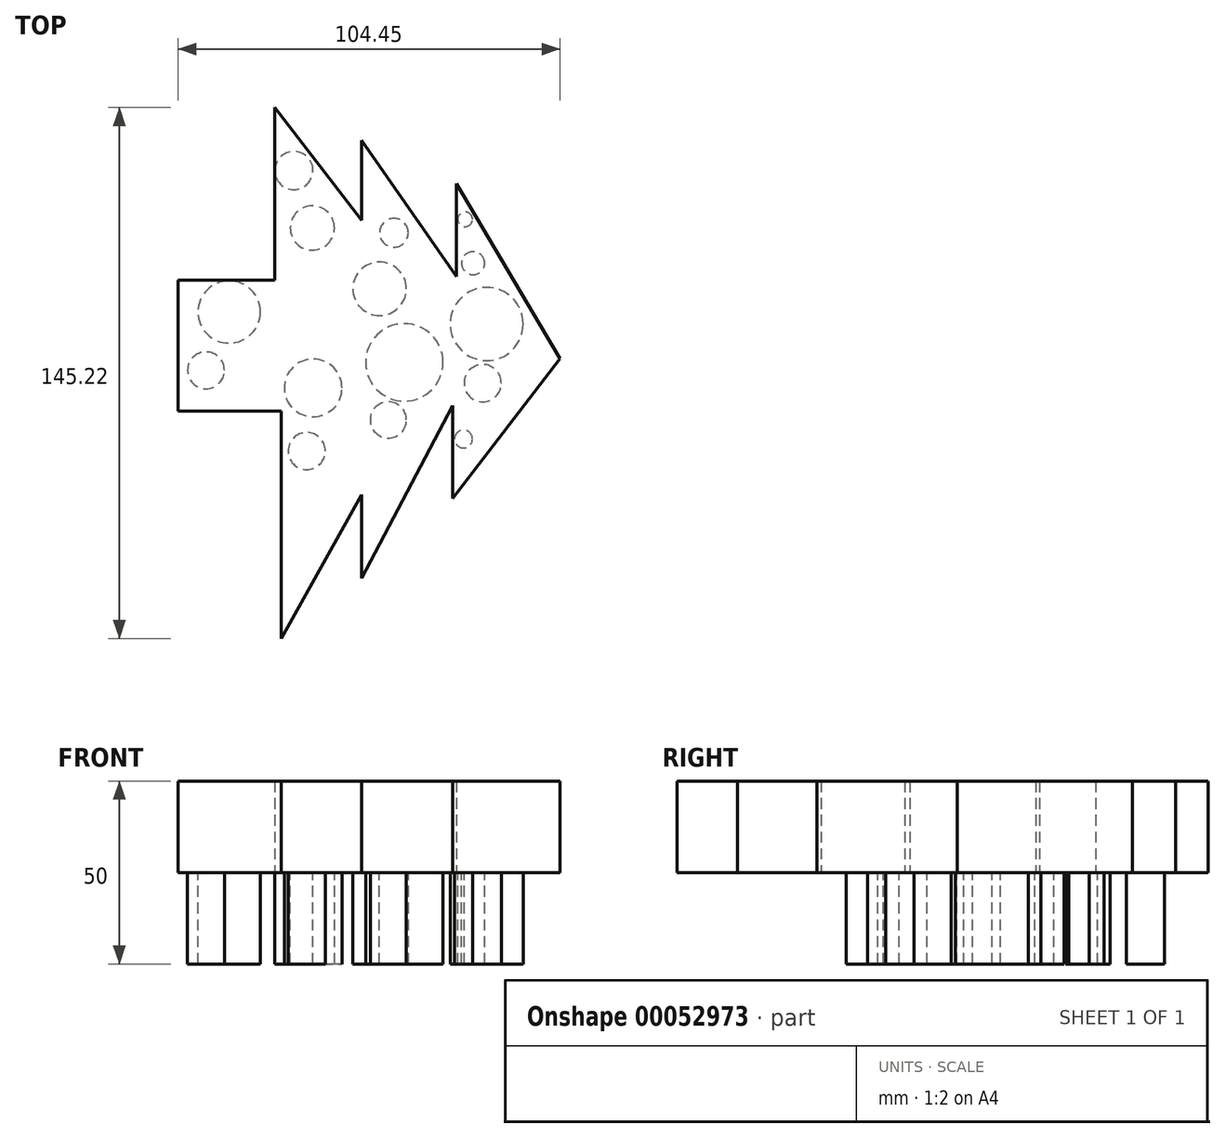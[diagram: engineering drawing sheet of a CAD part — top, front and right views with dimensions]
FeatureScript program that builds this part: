
annotation { "Feature Type Name" : "Feature", "Feature Type Description" : "" }
export const myFeature = defineFeature(function(context is Context, id is Id, definition is map)
    precondition{}
    {
        {
            var Q0;
            Q0=qCreatedBy(makeId("Top.planeOp"),FACE);
            var sketch = newSketch(context, id + "F0", { "sketchPlane" : qUnion([Q0])});
            skLineSegment(sketch, "E0", {"start": v(54.19, -5.72) * mm, "end": v(24.86, -44) * mm});
            skLineSegment(sketch, "E1", {"start": v(24.86, -44) * mm, "end": v(24.86, -18.6) * mm});
            skLineSegment(sketch, "E2", {"start": v(24.86, -18.6) * mm, "end": v(0, -65.81) * mm});
            skLineSegment(sketch, "E3", {"start": v(0, -65.81) * mm, "end": v(0, -42.92) * mm});
            skLineSegment(sketch, "E4", {"start": v(0, -42.92) * mm, "end": v(-22, -82.27) * mm});
            skLineSegment(sketch, "E5", {"start": v(-22, -82.27) * mm, "end": v(-22, -20.03) * mm});
            skLineSegment(sketch, "E6", {"start": v(-22, -20.03) * mm, "end": v(-50.26, -20.03) * mm});
            skLineSegment(sketch, "E7", {"start": v(-50.26, -20.03) * mm, "end": v(-50.26, 15.74) * mm});
            skLineSegment(sketch, "E8", {"start": v(-50.26, 15.74) * mm, "end": v(-23.79, 15.74) * mm});
            skLineSegment(sketch, "E9", {"start": v(-23.79, 15.74) * mm, "end": v(-23.79, 62.95) * mm});
            skLineSegment(sketch, "E10", {"start": v(-23.79, 62.95) * mm, "end": v(0, 32.2) * mm});
            skLineSegment(sketch, "E11", {"start": v(0, 32.2) * mm, "end": v(0, 54.01) * mm});
            skLineSegment(sketch, "E12", {"start": v(0, 54.01) * mm, "end": v(25.93, 16.81) * mm});
            skLineSegment(sketch, "E13", {"start": v(25.93, 16.81) * mm, "end": v(25.93, 42.2) * mm});
            skLineSegment(sketch, "E14", {"start": v(25.93, 42.2) * mm, "end": v(54.19, -5.72) * mm});
            skSolve(sketch);
        }
        {
            var Q0;
            Q0=makeQuery(id+"F0.imprint","IMPRINT",FACE,{"disambiguationData":[TD([[makeQuery(id+"F0.imprint","IMPRINT",EDGE,{"derivedFrom":sQuery(id+"F0.wireOp",EDGE,"E0")}),-1.0]])]});
            extrude(context, id + "F1", {"entities" : qUnion([Q0]), "depth" : 25 * mm});
        }
        {
            var Q0;
            Q0=qCreatedBy(makeId("Top.planeOp"),FACE);
            var sketch = newSketch(context, id + "F2", { "sketchPlane" : qUnion([Q0])});
            skCircle(sketch, "E15", {"center": v(4.86, 13.39) * mm, "radius": 7.3 * mm});
            skCircle(sketch, "E16", {"center": v(-36.23, 7.05) * mm, "radius": 8.51 * mm});
            skCircle(sketch, "E17", {"center": v(-13.28, -13.72) * mm, "radius": 7.88 * mm});
            skCircle(sketch, "E18", {"center": v(11.64, -6.72) * mm, "radius": 10.58 * mm});
            skCircle(sketch, "E19", {"center": v(34.16, 3.77) * mm, "radius": 9.99 * mm});
            skCircle(sketch, "E20", {"center": v(-18.53, 45.74) * mm, "radius": 5.21 * mm});
            skCircle(sketch, "E21", {"center": v(5.08, 38.96) * mm, "radius": 3.72 * mm});
            skCircle(sketch, "E22", {"center": v(28.25, 32.4) * mm, "radius": 2.02 * mm});
            skCircle(sketch, "E23", {"center": v(27.82, -27.7) * mm, "radius": 2.44 * mm});
            skCircle(sketch, "E24", {"center": v(3.33, -38.2) * mm, "radius": 5.34 * mm});
            skCircle(sketch, "E25", {"center": v(-15.25, -48.48) * mm, "radius": 6.91 * mm});
            skCircle(sketch, "E26", {"center": v(-42.57, -8.9) * mm, "radius": 5.03 * mm});
            skCircle(sketch, "E27", {"center": v(-19.84, 7.92) * mm, "radius": 6.3 * mm});
            skCircle(sketch, "E28", {"center": v(-13.5, 30) * mm, "radius": 6.05 * mm});
            skCircle(sketch, "E29", {"center": v(8.8, 28.7) * mm, "radius": 3.94 * mm});
            skCircle(sketch, "E30", {"center": v(30.44, 20.38) * mm, "radius": 3.15 * mm});
            skCircle(sketch, "E31", {"center": v(33.06, -12.4) * mm, "radius": 5.08 * mm});
            skCircle(sketch, "E32", {"center": v(7.27, -22.46) * mm, "radius": 4.95 * mm});
            skCircle(sketch, "E33", {"center": v(-15.03, -30.99) * mm, "radius": 5.1 * mm});
            skSolve(sketch);
        }
        {
            var Q0;
            Q0=makeQuery(id+"F2.imprint","IMPRINT",FACE,{"disambiguationData":[TD([[makeQuery(id+"F2.imprint","IMPRINT",EDGE,{"derivedFrom":sQuery(id+"F2.wireOp",EDGE,"E26")}),1.0]])]});
            var Q1;
            Q1=makeQuery(id+"F2.imprint","IMPRINT",FACE,{"disambiguationData":[TD([[makeQuery(id+"F2.imprint","IMPRINT",EDGE,{"derivedFrom":sQuery(id+"F2.wireOp",EDGE,"E28")}),1.0]])]});
            var Q2;
            Q2=makeQuery(id+"F2.imprint","IMPRINT",FACE,{"disambiguationData":[TD([[makeQuery(id+"F2.imprint","IMPRINT",EDGE,{"derivedFrom":sQuery(id+"F2.wireOp",EDGE,"E23")}),1.0]])]});
            var Q3;
            Q3=makeQuery(id+"F2.imprint","IMPRINT",FACE,{"disambiguationData":[TD([[makeQuery(id+"F2.imprint","IMPRINT",EDGE,{"derivedFrom":sQuery(id+"F2.wireOp",EDGE,"E20")}),1.0]])]});
            var Q4;
            Q4=makeQuery(id+"F2.imprint","IMPRINT",FACE,{"disambiguationData":[TD([[makeQuery(id+"F2.imprint","IMPRINT",EDGE,{"derivedFrom":sQuery(id+"F2.wireOp",EDGE,"E32")}),1.0]])]});
            var Q5;
            Q5=makeQuery(id+"F2.imprint","IMPRINT",FACE,{"disambiguationData":[TD([[makeQuery(id+"F2.imprint","IMPRINT",EDGE,{"derivedFrom":sQuery(id+"F2.wireOp",EDGE,"E19")}),1.0]])]});
            var Q6;
            Q6=makeQuery(id+"F2.imprint","IMPRINT",FACE,{"disambiguationData":[TD([[makeQuery(id+"F2.imprint","IMPRINT",EDGE,{"derivedFrom":sQuery(id+"F2.wireOp",EDGE,"E18")}),1.0]])]});
            var Q7;
            Q7=makeQuery(id+"F2.imprint","IMPRINT",FACE,{"disambiguationData":[TD([[makeQuery(id+"F2.imprint","IMPRINT",EDGE,{"derivedFrom":sQuery(id+"F2.wireOp",EDGE,"E33")}),1.0]])]});
            var Q8;
            Q8=makeQuery(id+"F2.imprint","IMPRINT",FACE,{"disambiguationData":[TD([[makeQuery(id+"F2.imprint","IMPRINT",EDGE,{"derivedFrom":sQuery(id+"F2.wireOp",EDGE,"E17")}),1.0]])]});
            var Q9;
            Q9=makeQuery(id+"F2.imprint","IMPRINT",FACE,{"disambiguationData":[TD([[makeQuery(id+"F2.imprint","IMPRINT",EDGE,{"derivedFrom":sQuery(id+"F2.wireOp",EDGE,"E16")}),1.0]])]});
            var Q10;
            Q10=makeQuery(id+"F2.imprint","IMPRINT",FACE,{"disambiguationData":[TD([[makeQuery(id+"F2.imprint","IMPRINT",EDGE,{"derivedFrom":sQuery(id+"F2.wireOp",EDGE,"E31")}),1.0]])]});
            var Q11;
            Q11=makeQuery(id+"F2.imprint","IMPRINT",FACE,{"disambiguationData":[TD([[makeQuery(id+"F2.imprint","IMPRINT",EDGE,{"derivedFrom":sQuery(id+"F2.wireOp",EDGE,"E15")}),1.0]])]});
            var Q12;
            Q12=makeQuery(id+"F2.imprint","IMPRINT",FACE,{"disambiguationData":[TD([[makeQuery(id+"F2.imprint","IMPRINT",EDGE,{"derivedFrom":sQuery(id+"F2.wireOp",EDGE,"E29")}),1.0]])]});
            var Q13;
            Q13=makeQuery(id+"F2.imprint","IMPRINT",FACE,{"disambiguationData":[TD([[makeQuery(id+"F2.imprint","IMPRINT",EDGE,{"derivedFrom":sQuery(id+"F2.wireOp",EDGE,"E30")}),1.0]])]});
            var Q14;
            Q14=makeQuery(id+"F2.imprint","IMPRINT",FACE,{"disambiguationData":[TD([[makeQuery(id+"F2.imprint","IMPRINT",EDGE,{"derivedFrom":sQuery(id+"F2.wireOp",EDGE,"E22")}),1.0]])]});
            extrude(context, id + "F3", {"entities" : qUnion([Q0, Q1, Q2, Q3, Q4, Q5, Q6, Q7, Q8, Q9, Q10, Q11, Q12, Q13, Q14]), "oppositeDirection" : true, "depth" : 25 * mm});
        }
    });
